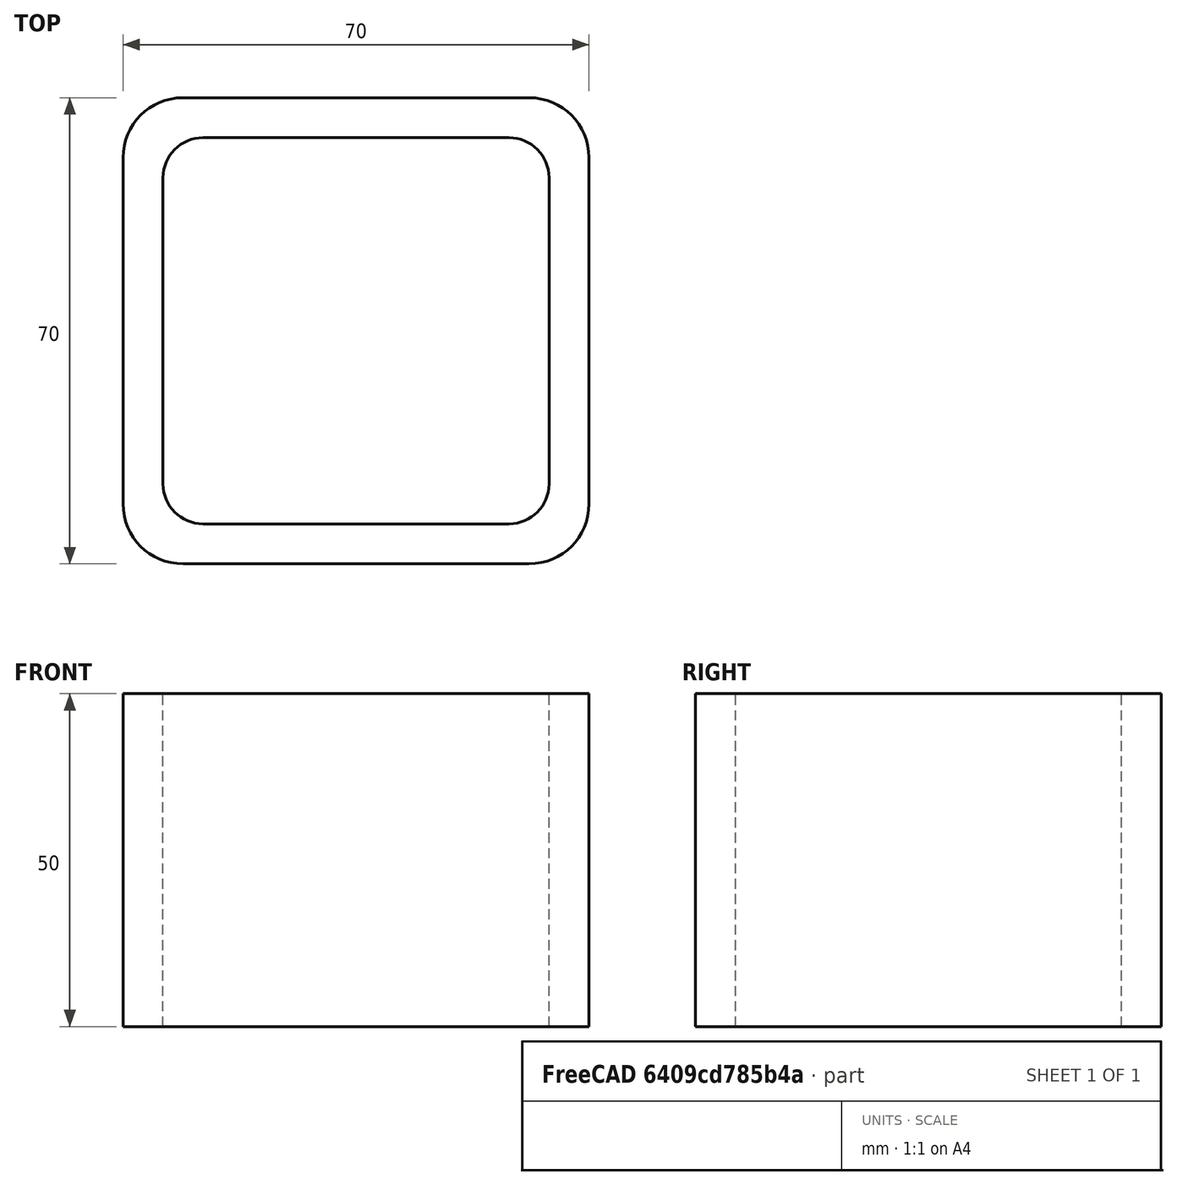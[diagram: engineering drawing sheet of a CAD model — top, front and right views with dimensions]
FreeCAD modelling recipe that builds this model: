
FCSTD DOCUMENT  (FreeCAD 0.15R4671 (Git))
Label: Square hollow section 70x70x6 EN10219 S235JRH
License: All rights reserved
LicenseURL: http://en.wikipedia.org/wiki/All_rights_reserved
objects: Sketcher::SketchObject×1, Part::Extrusion×1
note: 2 computed .brp shape members not serialized (recipe doc carries the construction recipe); baked Part::Feature solids carry a one-line shape summary decoded from their .brp

FEATURE [Sketcher::SketchObject] Sketch
  sketch-geometry (16):
    g0: LineSegment StartX=-23 StartY=29 StartZ=0 EndX=23 EndY=29 EndZ=0
    g1: LineSegment StartX=29 StartY=23 StartZ=0 EndX=29 EndY=-23 EndZ=0
    g2: LineSegment StartX=23 StartY=-29 StartZ=0 EndX=-23 EndY=-29 EndZ=0
    g3: LineSegment StartX=-29 StartY=-23 StartZ=0 EndX=-29 EndY=23 EndZ=0
    g4: LineSegment StartX=-26 StartY=35 StartZ=0 EndX=26 EndY=35 EndZ=0
    g5: LineSegment StartX=35 StartY=26 StartZ=0 EndX=35 EndY=-26 EndZ=0
    g6: LineSegment StartX=26 StartY=-35 StartZ=0 EndX=-26 EndY=-35 EndZ=0
    g7: LineSegment StartX=-35 StartY=-26 StartZ=0 EndX=-35 EndY=26 EndZ=0
    g8: ArcOfCircle CenterX=-23 CenterY=23 CenterZ=0 NormalX=0 NormalY=0 NormalZ=1 Radius=6 StartAngle=1.5708 EndAngle=3.14159
    g9: ArcOfCircle CenterX=23 CenterY=23 CenterZ=0 NormalX=0 NormalY=0 NormalZ=1 Radius=6 StartAngle=0 EndAngle=1.5708
    g10: ArcOfCircle CenterX=23 CenterY=-23 CenterZ=0 NormalX=0 NormalY=0 NormalZ=1 Radius=6 StartAngle=4.71239 EndAngle=6.28319
    g11: ArcOfCircle CenterX=-23 CenterY=-23 CenterZ=0 NormalX=0 NormalY=0 NormalZ=1 Radius=6 StartAngle=3.14159 EndAngle=4.71239
    g12: ArcOfCircle CenterX=26 CenterY=26 CenterZ=0 NormalX=0 NormalY=0 NormalZ=1 Radius=9 StartAngle=0 EndAngle=1.5708
    g13: ArcOfCircle CenterX=26 CenterY=-26 CenterZ=0 NormalX=0 NormalY=0 NormalZ=1 Radius=9 StartAngle=4.71239 EndAngle=6.28319
    g14: ArcOfCircle CenterX=-26 CenterY=-26 CenterZ=0 NormalX=0 NormalY=0 NormalZ=1 Radius=9 StartAngle=3.14159 EndAngle=4.71239
    g15: ArcOfCircle CenterX=-26 CenterY=26 CenterZ=0 NormalX=0 NormalY=0 NormalZ=1 Radius=9 StartAngle=1.5708 EndAngle=3.14159
  constraints (36):
    c: Horizontal(g2)
    c: Vertical(g3)
    c: Horizontal(g6)
    c: Vertical(g7)
    c: Tangent(g3,g8) = 1.5708
    c: Tangent(g0,g8) = 1.5708
    c: Tangent(g0,g9) = 1.5708
    c: Tangent(g1,g9) = 1.5708
    c: Tangent(g1,g10) = 1.5708
    c: Tangent(g2,g10) = 1.5708
    c: Tangent(g2,g11) = 1.5708
    c: Tangent(g3,g11) = 1.5708
    c: Tangent(g4,g12) = 1.5708
    c: Tangent(g5,g12) = 1.5708
    c: Tangent(g5,g13) = 1.5708
    c: Tangent(g6,g13) = 1.5708
    c: Tangent(g6,g14) = 1.5708
    c: Tangent(g7,g14) = 1.5708
    c: Tangent(g7,g15) = 1.5708
    c: Tangent(g4,g15) = 1.5708
    c: Equal(g9,g8)
    c: Equal(g9,g11)
    c: Equal(g9,g10)
    c: Equal(g12,g15)
    c: Equal(g12,g14)
    c: Equal(g12,g13)
    c: Symmetric(g4,g6,g-1)
    c: Symmetric(g7,g5,g-2)
    c: DistanceY(g4,g6) = -70
    c: DistanceX(g7,g5) = 70
    c: Symmetric(g3,g1,g-2)
    c: Symmetric(g0,g2,g-1)
    c: DistanceY(g0,g4) = 6
    c: DistanceX(g5,g1) = -6
    c: Radius(g9) = 6
    c: Radius(g12) = 9
FEATURE [Part::Extrusion] Extrude  label="Square hollow section 70x70x6 EN10219 S235JRH"
  Base = -> Sketch
  Dir = (0,0,50)
  Solid = true
